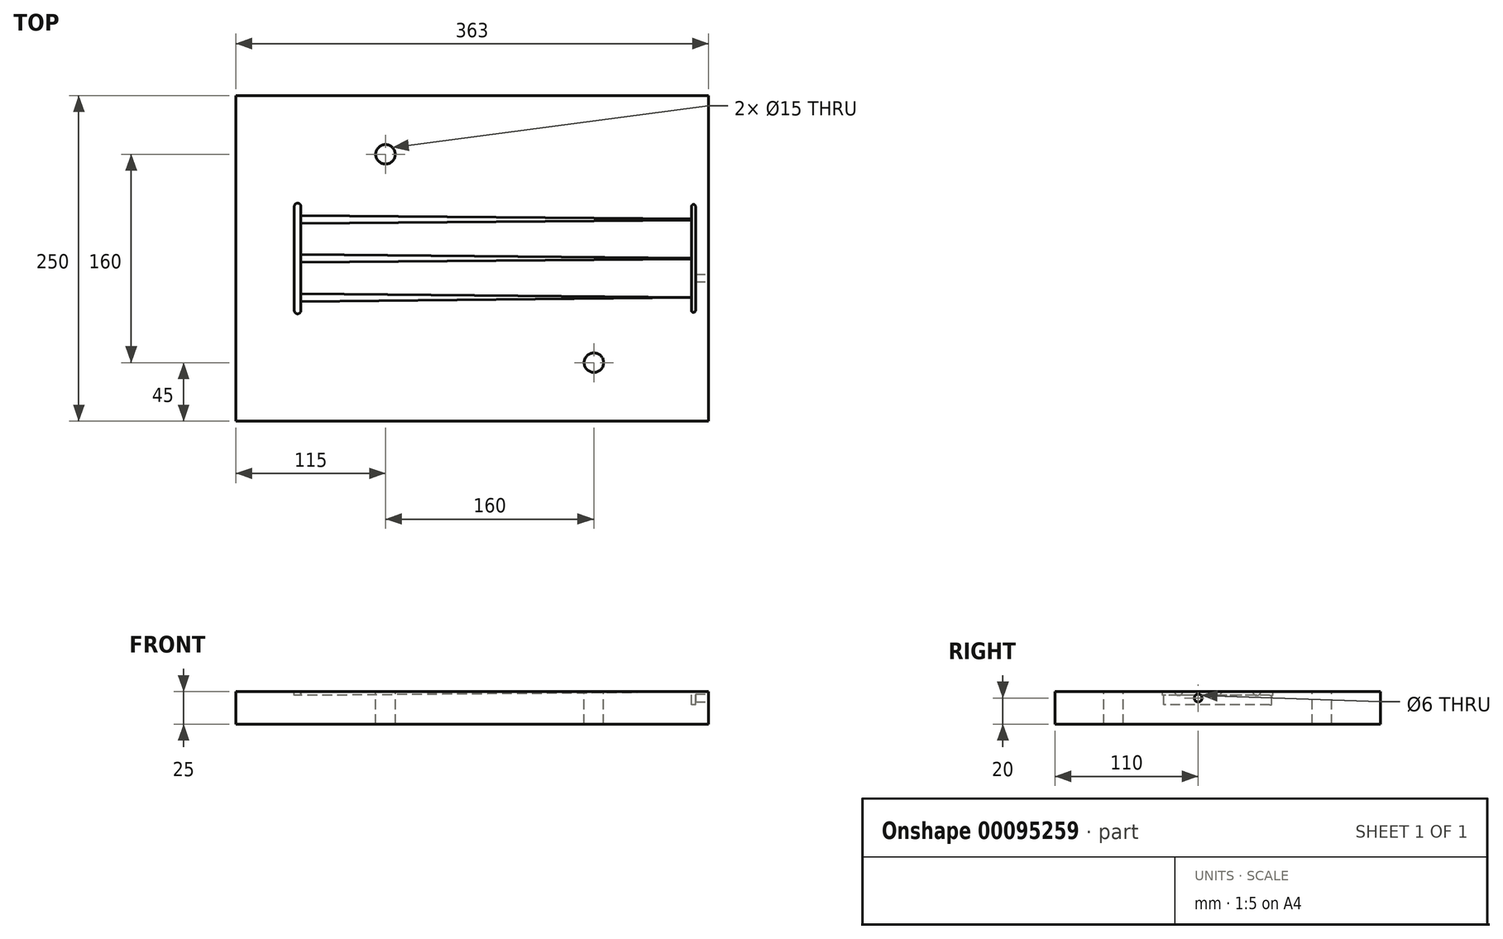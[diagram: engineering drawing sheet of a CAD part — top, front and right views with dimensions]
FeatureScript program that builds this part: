
annotation { "Feature Type Name" : "Feature", "Feature Type Description" : "" }
export const myFeature = defineFeature(function(context is Context, id is Id, definition is map)
    precondition{}
    {
        {
            var Q0;
            Q0=qCreatedBy(makeId("Top.planeOp"),FACE);
            var sketch = newSketch(context, id + "F0", { "sketchPlane" : qUnion([Q0])});
            skLineSegment(sketch, "E0.bottom", {"start": v(175, 125) * mm, "end": v(-175, 125) * mm});
            skLineSegment(sketch, "E0.top", {"start": v(175, -125) * mm, "end": v(-175, -125) * mm});
            skLineSegment(sketch, "E0.left", {"start": v(175, 125) * mm, "end": v(175, -125) * mm});
            skLineSegment(sketch, "E0.right", {"start": v(-175, 125) * mm, "end": v(-175, -125) * mm});
            skPoint(sketch, "E0.middle", {"position": v(0, 0) * mm});
            skSolve(sketch);
        }
        {
            var Q0;
            Q0=qSketchRegion(id+"F0",true);
            extrude(context, id + "F1", {"entities" : qUnion([Q0]), "depth" : 25 * mm});
        }
        {
            var Q0;
            Q0=makeQuery(id+"F1.opExtrude","CAP_FACE",FACE,{"disambiguationData":[OSD([sQuery(id+"F0.wireOp",EDGE,"E0.bottom"),sQuery(id+"F0.wireOp",EDGE,"E0.top"),sQuery(id+"F0.wireOp",EDGE,"E0.left"),sQuery(id+"F0.wireOp",EDGE,"E0.right")])],"isStart":false});
            var sketch = newSketch(context, id + "F2", { "sketchPlane" : qUnion([Q0])});
            skLineSegment(sketch, "E1", {"start": v(175, 0.25) * mm, "end": v(-125, 3) * mm});
            skLineSegment(sketch, "E2", {"start": v(-125, 3) * mm, "end": v(-125, 0) * mm});
            skLineSegment(sketch, "E3", {"start": v(-125, 0) * mm, "end": v(175, 0) * mm});
            skLineSegment(sketch, "E4", {"start": v(175, 0.25) * mm, "end": v(175, 0) * mm});
            skSolve(sketch);
        }
        {
            var Q0;
            Q0=qSketchRegion(id+"F2",true);
            var Q1;
            Q1=sQuery(id+"F2.wireOp",EDGE,"E3");
            revolve(context, id + "F3", {"operationType" : NewBodyOperationType.REMOVE, "entities" : qUnion([Q0]), "axis" : qUnion([Q1]), "revolveType" : RevolveType.FULL, "oppositeDirection" : true});
        }
        {
            var Q0;
            Q0=makeQuery(id+"F1.opExtrude","CAP_FACE",FACE,{"disambiguationData":[OSD([sQuery(id+"F0.wireOp",EDGE,"E0.bottom"),sQuery(id+"F0.wireOp",EDGE,"E0.top"),sQuery(id+"F0.wireOp",EDGE,"E0.left"),sQuery(id+"F0.wireOp",EDGE,"E0.right")])],"isStart":false});
            var sketch = newSketch(context, id + "F4", { "sketchPlane" : qUnion([Q0])});
            skCircle(sketch, "E5", {"center": v(100, -80) * mm, "radius": 7.5 * mm});
            skCircle(sketch, "E6", {"center": v(100, -80) * mm, "radius": 5 * mm});
            skCircle(sketch, "E7", {"center": v(-60, 80) * mm, "radius": 5 * mm});
            skCircle(sketch, "E8", {"center": v(-60, 80) * mm, "radius": 7.5 * mm});
            skSolve(sketch);
        }
        {
            var Q0;
            Q0=makeQuery(id+"F4.imprint","IMPRINT",FACE,{"disambiguationData":[TD([[makeQuery(id+"F4.imprint","IMPRINT",EDGE,{"derivedFrom":sQuery(id+"F4.wireOp",EDGE,"E7")}),-1.0]])]});
            var Q1;
            Q1=makeQuery(id+"F4.imprint","IMPRINT",FACE,{"disambiguationData":[TD([[makeQuery(id+"F4.imprint","IMPRINT",EDGE,{"derivedFrom":sQuery(id+"F4.wireOp",EDGE,"E7")}),1.0]])]});
            var Q2;
            Q2=makeQuery(id+"F4.imprint","IMPRINT",FACE,{"disambiguationData":[TD([[makeQuery(id+"F4.imprint","IMPRINT",EDGE,{"derivedFrom":sQuery(id+"F4.wireOp",EDGE,"E5")}),1.0]])]});
            var Q3;
            Q3=makeQuery(id+"F4.imprint","IMPRINT",FACE,{"disambiguationData":[TD([[makeQuery(id+"F4.imprint","IMPRINT",EDGE,{"derivedFrom":sQuery(id+"F4.wireOp",EDGE,"E6")}),1.0]])]});
            extrude(context, id + "F5", {"entities" : qUnion([Q0, Q1, Q2, Q3]), "operationType" : NewBodyOperationType.REMOVE, "endBound" : BoundingType.THROUGH_ALL, "oppositeDirection" : true, "depth" : 15 * mm});
        }
        {
            var Q0;
            {var subQ0=sQuery(id+"F0.wireOp",EDGE,"E0.right");var subQ1=sQuery(id+"F0.wireOp",EDGE,"E0.left");var subQ2=sQuery(id+"F0.wireOp",EDGE,"E0.top");var subQ3=sQuery(id+"F0.wireOp",EDGE,"E0.bottom");Q0=makeQuery(id+"F5.boolean.opBoolean","SPLIT",FACE,{"disambiguationData":[TD([makeQuery(id+"F1.opExtrude","SWEPT_FACE",FACE,{"disambiguationData":[OSD([subQ3])]})])],"derivedFrom":makeQuery(id+"F1.opExtrude","CAP_FACE",FACE,{"disambiguationData":[OSD([subQ3,subQ2,subQ1,subQ0])],"isStart":false})});}
            var sketch = newSketch(context, id + "F6", { "sketchPlane" : qUnion([Q0])});
            skLineSegment(sketch, "E9", {"start": v(-125, 30) * mm, "end": v(175, 30) * mm});
            skLineSegment(sketch, "E10", {"start": v(175, 30) * mm, "end": v(175, 30.5) * mm});
            skLineSegment(sketch, "E11", {"start": v(175, 30.5) * mm, "end": v(-125, 33) * mm});
            skLineSegment(sketch, "E12", {"start": v(-125, 33) * mm, "end": v(-125, 30) * mm});
            skLineSegment(sketch, "E13.MirrorCS", {"start": v(-125, -30) * mm, "end": v(175, -30) * mm});
            skLineSegment(sketch, "E14.MirrorCS", {"start": v(175, -30.5) * mm, "end": v(-125, -33) * mm});
            skLineSegment(sketch, "E15.MirrorCS", {"start": v(-125, -33) * mm, "end": v(-125, -30) * mm});
            skLineSegment(sketch, "E16.MirrorCS", {"start": v(175, -30) * mm, "end": v(175, -30.5) * mm});
            skSolve(sketch);
        }
        {
            var Q0;
            Q0=makeQuery(id+"F6.imprint","IMPRINT",FACE,{"disambiguationData":[TD([[makeQuery(id+"F6.imprint","IMPRINT",EDGE,{"derivedFrom":sQuery(id+"F6.wireOp",EDGE,"E9")}),1.0]])]});
            var Q1;
            Q1=sQuery(id+"F6.wireOp",EDGE,"E9");
            revolve(context, id + "F7", {"operationType" : NewBodyOperationType.REMOVE, "entities" : qUnion([Q0]), "axis" : qUnion([Q1]), "revolveType" : RevolveType.FULL, "oppositeDirection" : true});
        }
        {
            var Q0;
            {var subQ0=sQuery(id+"F0.wireOp",EDGE,"E0.right");var subQ1=sQuery(id+"F0.wireOp",EDGE,"E0.left");var subQ2=sQuery(id+"F0.wireOp",EDGE,"E0.top");var subQ3=sQuery(id+"F0.wireOp",EDGE,"E0.bottom");Q0=makeQuery(id+"F5.boolean.opBoolean","SPLIT",FACE,{"disambiguationData":[TD([makeQuery(id+"F1.opExtrude","SWEPT_FACE",FACE,{"disambiguationData":[OSD([subQ3])]})])],"derivedFrom":makeQuery(id+"F1.opExtrude","CAP_FACE",FACE,{"disambiguationData":[OSD([subQ3,subQ2,subQ1,subQ0])],"isStart":false})});}
            var sketch = newSketch(context, id + "F8", { "sketchPlane" : qUnion([Q0])});
            skLineSegment(sketch, "E17", {"start": v(-125, -30) * mm, "end": v(-125, -33) * mm});
            skLineSegment(sketch, "E18", {"start": v(-125, -33) * mm, "end": v(175, -30.05) * mm});
            skLineSegment(sketch, "E19", {"start": v(175, -30.05) * mm, "end": v(175, -30) * mm});
            skLineSegment(sketch, "E20", {"start": v(175, -30) * mm, "end": v(-125, -30) * mm});
            skSolve(sketch);
        }
        {
            var Q0;
            Q0 = qSketchRegion(id + "F8", true);
            var Q1;
            Q1=sQuery(id+"F8.wireOp",EDGE,"E20");
            revolve(context, id + "F9", {"operationType" : NewBodyOperationType.REMOVE, "entities" : qUnion([Q0]), "axis" : qUnion([Q1]), "revolveType" : RevolveType.FULL, "oppositeDirection" : true});
        }
        {
            var Q0;
            {var subQ0=sQuery(id+"F0.wireOp",EDGE,"E0.right");var subQ1=sQuery(id+"F0.wireOp",EDGE,"E0.left");var subQ2=sQuery(id+"F0.wireOp",EDGE,"E0.top");var subQ3=sQuery(id+"F0.wireOp",EDGE,"E0.bottom");Q0=makeQuery(id+"F5.boolean.opBoolean","SPLIT",FACE,{"disambiguationData":[TD([makeQuery(id+"F1.opExtrude","SWEPT_FACE",FACE,{"disambiguationData":[OSD([subQ3])]})])],"derivedFrom":makeQuery(id+"F1.opExtrude","CAP_FACE",FACE,{"disambiguationData":[OSD([subQ3,subQ2,subQ1,subQ0])],"isStart":false})});}
            var sketch = newSketch(context, id + "F10", { "sketchPlane" : qUnion([Q0])});
            skLineSegment(sketch, "E21.bottom", {"start": v(-125, 40) * mm, "end": v(-130, 40) * mm});
            skLineSegment(sketch, "E21.top", {"start": v(-125, -40) * mm, "end": v(-130, -40) * mm});
            skLineSegment(sketch, "E21.left", {"start": v(-125, 40) * mm, "end": v(-125, -40) * mm});
            skLineSegment(sketch, "E21.right", {"start": v(-130, 40) * mm, "end": v(-130, -40) * mm});
            skArc(sketch, "E22", {"start": v(-130, 40) * mm, "mid": v(-127.5, 42.5) * mm, "end": v(-125, 40) * mm});
            skArc(sketch, "E23", {"start": v(-130, -40) * mm, "mid": v(-127.5, -42.5) * mm, "end": v(-125, -40) * mm});
            skSolve(sketch);
        }
        {
            var Q0;
            Q0 = qSketchRegion(id + "F10", true);
            extrude(context, id + "F11", {"entities" : qUnion([Q0]), "operationType" : NewBodyOperationType.REMOVE, "oppositeDirection" : true, "depth" : 3 * mm});
        }
        {
            var Q0;
            Q0=qCreatedBy(makeId("Top.planeOp"),FACE);
            var sketch = newSketch(context, id + "F12", { "sketchPlane" : qUnion([Q0])});
            skLineSegment(sketch, "E24.bottom", {"start": v(175, -125) * mm, "end": v(188, -125) * mm});
            skLineSegment(sketch, "E24.top", {"start": v(175, 125) * mm, "end": v(188, 125) * mm});
            skLineSegment(sketch, "E24.left", {"start": v(175, -125) * mm, "end": v(175, 125) * mm});
            skLineSegment(sketch, "E24.right", {"start": v(188, -125) * mm, "end": v(188, 125) * mm});
            skSolve(sketch);
        }
        {
            var Q0;
            Q0 = qSketchRegion(id + "F12", true);
            extrude(context, id + "F13", {"entities" : qUnion([Q0]), "operationType" : NewBodyOperationType.ADD, "depth" : 25 * mm});
        }
        {
            var Q0;
            {var subQ0=makeQuery(id+"F11.opExtrude","SWEPT_FACE",FACE,{"disambiguationData":[OSD([sQuery(id+"F10.wireOp",EDGE,"E21.left")])]});var subQ1=makeQuery(id+"F9.boolean.opBoolean","COPY",FACE,{"derivedFrom":makeQuery(id+"F9.opRevolve","SWEPT_FACE",FACE,{"disambiguationData":[OSD([sQuery(id+"F8.wireOp",EDGE,"E18")])]})});var subQ2=sQuery(id+"F0.wireOp",EDGE,"E0.right");var subQ3=makeQuery(id+"F1.opExtrude","SWEPT_FACE",FACE,{"disambiguationData":[OSD([subQ2])]});var subQ4=makeQuery(id+"F5.opExtrude","SWEPT_FACE",FACE,{"disambiguationData":[OSD([sQuery(id+"F4.wireOp",EDGE,"E5")])]});var subQ5=sQuery(id+"F0.wireOp",EDGE,"E0.bottom");var subQ6=makeQuery(id+"F1.opExtrude","SWEPT_FACE",FACE,{"disambiguationData":[OSD([subQ5])]});var subQ7=makeQuery(id+"F5.opExtrude","SWEPT_FACE",FACE,{"disambiguationData":[OSD([sQuery(id+"F4.wireOp",EDGE,"E8")])]});var subQ8=makeQuery(id+"F7.boolean.opBoolean","COPY",FACE,{"derivedFrom":makeQuery(id+"F7.opRevolve","SWEPT_FACE",FACE,{"disambiguationData":[OSD([sQuery(id+"F6.wireOp",EDGE,"E11")])]})});var subQ9=sQuery(id+"F0.wireOp",EDGE,"E0.top");var subQ10=makeQuery(id+"F1.opExtrude","SWEPT_FACE",FACE,{"disambiguationData":[OSD([subQ9])]});var subQ11=sQuery(id+"F0.wireOp",EDGE,"E0.left");var subQ12=makeQuery(id+"F1.opExtrude","SWEPT_FACE",FACE,{"disambiguationData":[OSD([subQ11])]});var subQ13=makeQuery(id+"F3.boolean.opBoolean","COPY",FACE,{"derivedFrom":makeQuery(id+"F3.opRevolve","SWEPT_FACE",FACE,{"disambiguationData":[OSD([sQuery(id+"F2.wireOp",EDGE,"E1")])]})});var subQ14=makeQuery(id+"F5.boolean.opBoolean","SPLIT",FACE,{"disambiguationData":[TD([subQ6])],"derivedFrom":makeQuery(id+"F1.opExtrude","CAP_FACE",FACE,{"disambiguationData":[OSD([subQ5,subQ9,subQ11,subQ2])],"isStart":false})});Q0=makeQuery(id+"F13.boolean.opBoolean","MERGE",FACE,{"derivedFrom":[makeQuery(id+"F11.boolean.opBoolean","SPLIT",FACE,{"disambiguationData":[TD([subQ12,subQ13,subQ8,subQ0])],"derivedFrom":subQ14}),makeQuery(id+"F11.boolean.opBoolean","SPLIT",FACE,{"disambiguationData":[TD([subQ12,subQ13,subQ1,subQ0])],"derivedFrom":subQ14}),makeQuery(id+"F11.boolean.opBoolean","SPLIT",FACE,{"disambiguationData":[TD([subQ6,subQ10,subQ12,subQ3,subQ4,subQ7,subQ8,subQ1,subQ0,makeQuery(id+"F11.opExtrude","SWEPT_FACE",FACE,{"disambiguationData":[OSD([sQuery(id+"F10.wireOp",EDGE,"E21.right")])]}),makeQuery(id+"F11.opExtrude","SWEPT_FACE",FACE,{"disambiguationData":[OSD([sQuery(id+"F10.wireOp",EDGE,"E22")])]}),makeQuery(id+"F11.opExtrude","SWEPT_FACE",FACE,{"disambiguationData":[OSD([sQuery(id+"F10.wireOp",EDGE,"E23")])]})])],"derivedFrom":subQ14}),makeQuery(id+"F13.opExtrude","CAP_FACE",FACE,{"disambiguationData":[OSD([sQuery(id+"F12.wireOp",EDGE,"E24.bottom"),sQuery(id+"F12.wireOp",EDGE,"E24.top"),sQuery(id+"F12.wireOp",EDGE,"E24.left"),sQuery(id+"F12.wireOp",EDGE,"E24.right")])],"isStart":false})]});}
            var sketch = newSketch(context, id + "F14", { "sketchPlane" : qUnion([Q0])});
            skLineSegment(sketch, "E25.bottom", {"start": v(175, 40) * mm, "end": v(178, 40) * mm});
            skLineSegment(sketch, "E25.top", {"start": v(175, -40) * mm, "end": v(178, -40) * mm});
            skLineSegment(sketch, "E25.left", {"start": v(175, 40) * mm, "end": v(175, -40) * mm});
            skLineSegment(sketch, "E25.right", {"start": v(178, 40) * mm, "end": v(178, -40) * mm});
            skArc(sketch, "E26", {"start": v(175, 40) * mm, "mid": v(176.5, 41.5) * mm, "end": v(178, 40) * mm});
            skArc(sketch, "E27", {"start": v(178, -40) * mm, "mid": v(176.5, -41.5) * mm, "end": v(175, -40) * mm});
            skSolve(sketch);
        }
        {
            var Q0;
            Q0 = qSketchRegion(id + "F14", true);
            extrude(context, id + "F15", {"entities" : qUnion([Q0]), "operationType" : NewBodyOperationType.REMOVE, "oppositeDirection" : true, "depth" : 10 * mm});
        }
        {
            var Q0;
            Q0=makeQuery(id+"F13.opExtrude","SWEPT_FACE",FACE,{"disambiguationData":[OSD([sQuery(id+"F12.wireOp",EDGE,"E24.right")])]});
            var sketch = newSketch(context, id + "F16", { "sketchPlane" : qUnion([Q0])});
            skCircle(sketch, "E28", {"center": v(-15, 20) * mm, "radius": 3 * mm});
            skSolve(sketch);
        }
        {
            var Q0;
            Q0 = qSketchRegion(id + "F16", true);
            extrude(context, id + "F17", {"entities" : qUnion([Q0]), "operationType" : NewBodyOperationType.REMOVE, "endBound" : BoundingType.UP_TO_NEXT, "oppositeDirection" : true, "depth" : 25 * mm});
        }
    });
